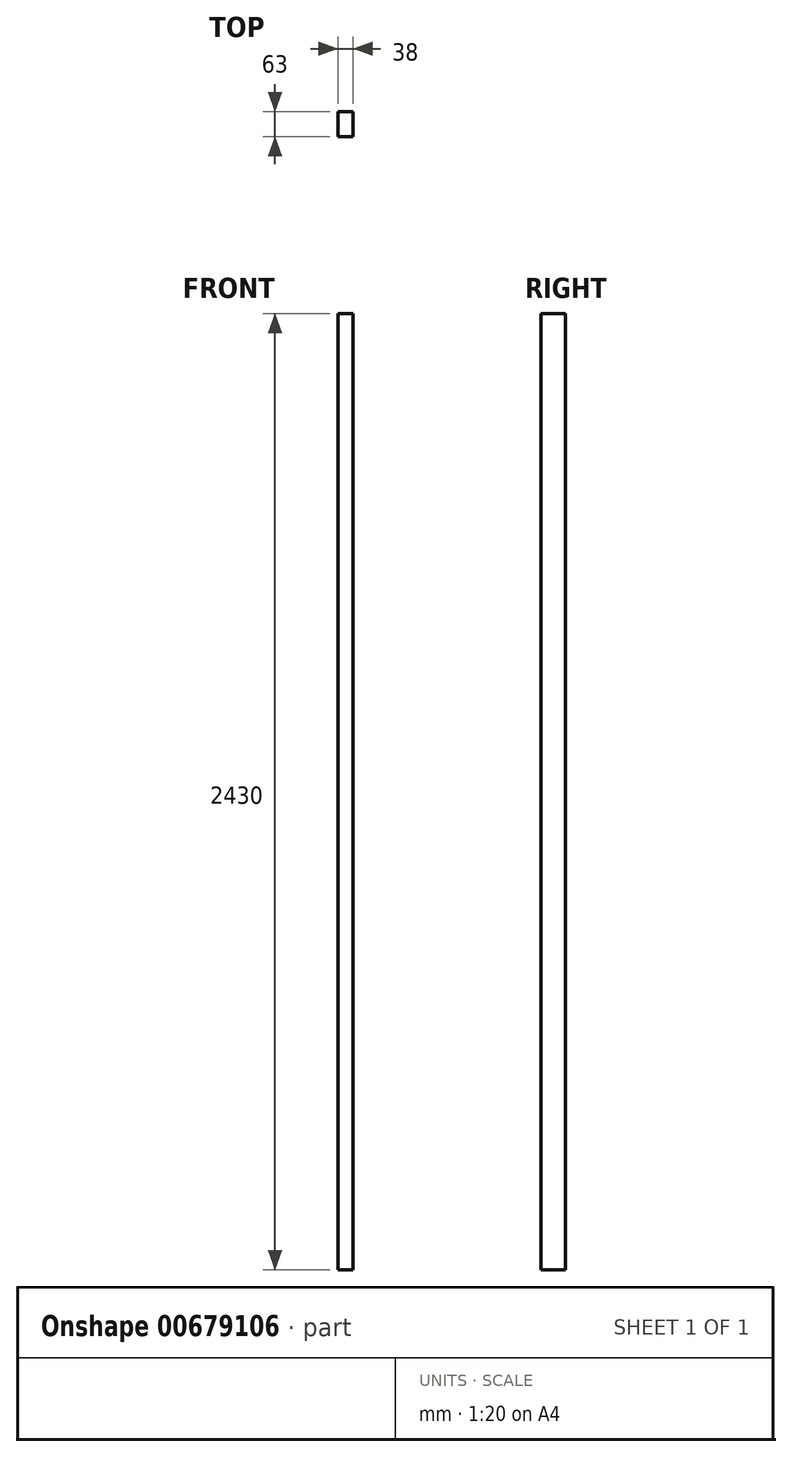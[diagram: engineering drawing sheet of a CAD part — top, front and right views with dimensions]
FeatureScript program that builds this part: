
annotation { "Feature Type Name" : "Feature", "Feature Type Description" : "" }
export const myFeature = defineFeature(function(context is Context, id is Id, definition is map)
    precondition{}
    {
        {
            var Q0;
            Q0=qCreatedBy(makeId("Top.planeOp"),FACE);
            var sketch = newSketch(context, id + "F0", { "sketchPlane" : qUnion([Q0])});
            skLineSegment(sketch, "E0.bottom", {"start": v(0, 0) * mm, "end": v(38, 0) * mm});
            skLineSegment(sketch, "E0.top", {"start": v(0, -63) * mm, "end": v(38, -63) * mm});
            skLineSegment(sketch, "E0.left", {"start": v(0, 0) * mm, "end": v(0, -63) * mm});
            skLineSegment(sketch, "E0.right", {"start": v(38, 0) * mm, "end": v(38, -63) * mm});
            skSolve(sketch);
        }
        {
            var Q0;
            Q0 = qSketchRegion(id + "F0", true);
            extrude(context, id + "F1", {"entities" : qUnion([Q0]), "depth" : 2430 * mm, "offsetDistance" : 25 * mm});
        }
    });
